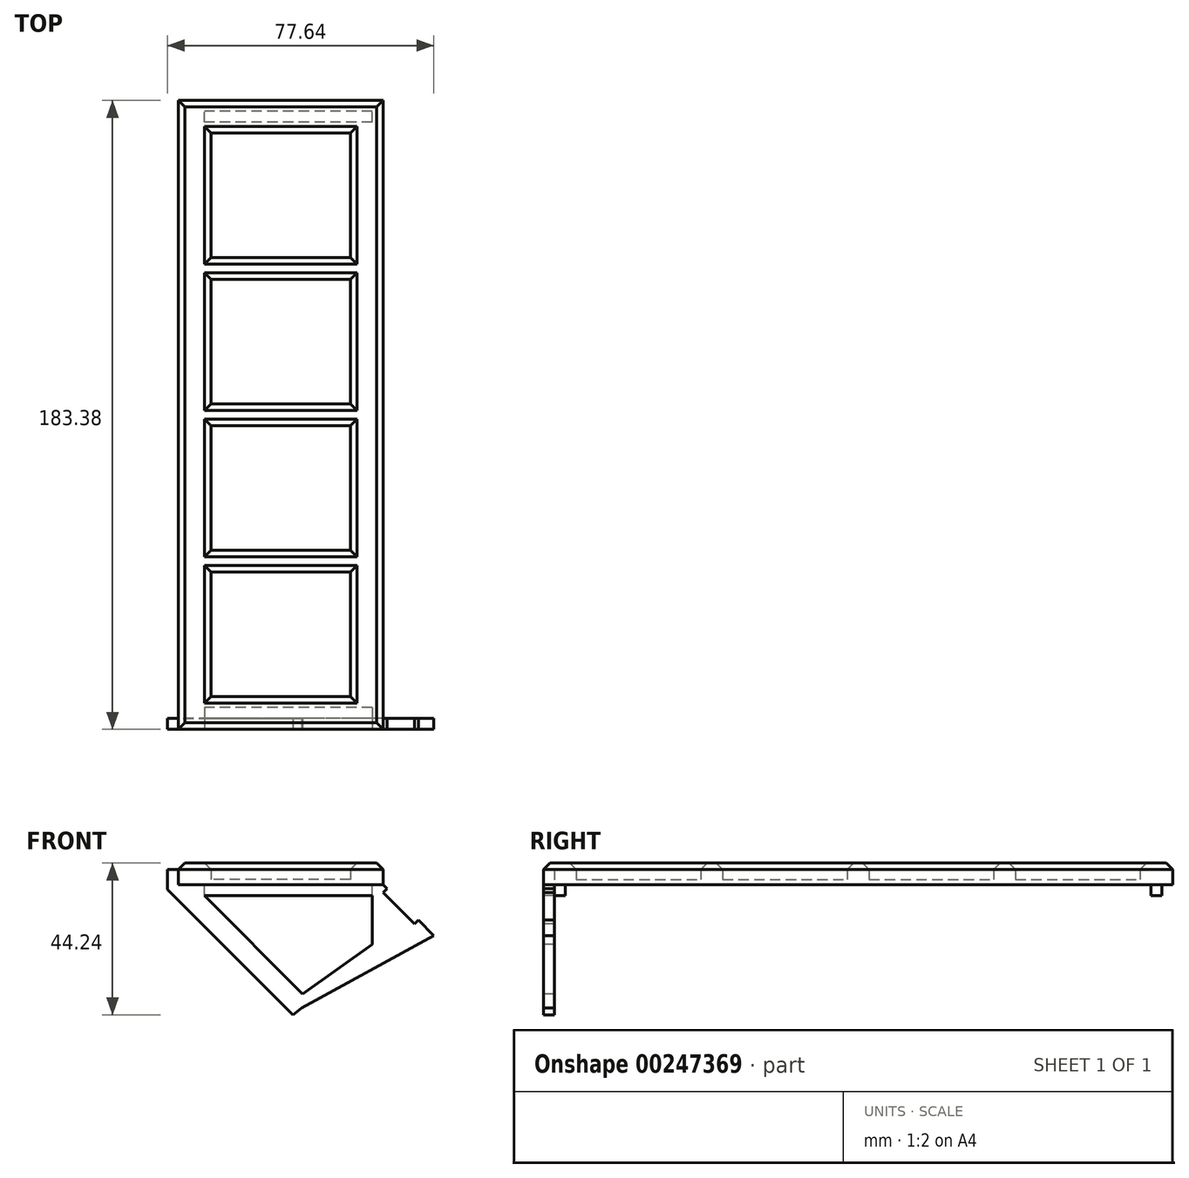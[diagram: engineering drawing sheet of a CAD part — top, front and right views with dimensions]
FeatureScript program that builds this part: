
annotation { "Feature Type Name" : "Feature", "Feature Type Description" : "" }
export const myFeature = defineFeature(function(context is Context, id is Id, definition is map)
    precondition{}
    {
        {
            var Q0;
            Q0=qCreatedBy(makeId("Top.planeOp"),FACE);
            var sketch = newSketch(context, id + "F0", { "sketchPlane" : qUnion([Q0])});
            skLineSegment(sketch, "E0.bottom", {"start": v(20.32, -82.17) * mm, "end": v(-20.32, -82.17) * mm});
            skLineSegment(sketch, "E0.top", {"start": v(20.32, 82.17) * mm, "end": v(-20.32, 82.17) * mm});
            skLineSegment(sketch, "E0.left", {"start": v(20.32, -82.17) * mm, "end": v(20.32, 82.17) * mm});
            skLineSegment(sketch, "E0.right", {"start": v(-20.32, -82.17) * mm, "end": v(-20.32, 82.17) * mm});
            skPoint(sketch, "E0.middle", {"position": v(0, 0) * mm});
            skLineSegment(sketch, "E1.0", {"start": v(-29.85, -91.7) * mm, "end": v(-29.85, 91.7) * mm});
            skLineSegment(sketch, "E1.1", {"start": v(29.84, -91.7) * mm, "end": v(-29.85, -91.7) * mm});
            skLineSegment(sketch, "E1.2", {"start": v(29.84, -91.7) * mm, "end": v(29.85, 91.7) * mm});
            skLineSegment(sketch, "E1.3", {"start": v(29.85, 91.7) * mm, "end": v(-29.85, 91.7) * mm});
            skLineSegment(sketch, "E2.0", {"start": v(20.32, -45.85) * mm, "end": v(-20.32, -45.85) * mm});
            skLineSegment(sketch, "E3.0", {"start": v(20.32, -3.18) * mm, "end": v(-20.32, -3.18) * mm});
            skLineSegment(sketch, "E4.0", {"start": v(20.32, 3.17) * mm, "end": v(-20.32, 3.17) * mm});
            skLineSegment(sketch, "E5.0", {"start": v(20.32, 39.5) * mm, "end": v(-20.32, 39.5) * mm});
            skLineSegment(sketch, "E6.0", {"start": v(20.32, 45.85) * mm, "end": v(-20.32, 45.85) * mm});
            skLineSegment(sketch, "E7.0", {"start": v(20.32, -39.5) * mm, "end": v(-20.32, -39.5) * mm});
            skSolve(sketch);
        }
        {
            var Q0;
            {var subQ5=sQuery(id+"F0.wireOp",EDGE,"E0.bottom");Q0=makeQuery(id+"F0.imprint","IMPRINT",FACE,{"disambiguationData":[TD([[makeQuery(id+"F0.imprint","IMPRINT",EDGE,{"derivedFrom":subQ5}),1.0]])]});}
            var Q1;
            {var subQ0=sQuery(id+"F0.wireOp",EDGE,"E3.0");Q1=makeQuery(id+"F0.imprint","IMPRINT",FACE,{"disambiguationData":[TD([[makeQuery(id+"F0.imprint","IMPRINT",EDGE,{"derivedFrom":subQ0}),-1.0]])]});}
            var Q2;
            {var subQ0=sQuery(id+"F0.wireOp",EDGE,"E2.0");Q2=makeQuery(id+"F0.imprint","IMPRINT",FACE,{"disambiguationData":[TD([[makeQuery(id+"F0.imprint","IMPRINT",EDGE,{"derivedFrom":subQ0}),-1.0]])]});}
            var Q3;
            {var subQ0=sQuery(id+"F0.wireOp",EDGE,"E5.0");Q3=makeQuery(id+"F0.imprint","IMPRINT",FACE,{"disambiguationData":[TD([[makeQuery(id+"F0.imprint","IMPRINT",EDGE,{"derivedFrom":subQ0}),-1.0]])]});}
            extrude(context, id + "F1", {"entities" : qUnion([Q0, Q1, Q2, Q3]), "depth" : 6.35 * mm});
        }
        {
            var Q0;
            Q0=makeQuery(id+"F1.opExtrude","CAP_FACE",FACE,{"disambiguationData":[OSD([sQuery(id+"F0.wireOp",EDGE,"E0.bottom"),sQuery(id+"F0.wireOp",EDGE,"E0.top"),sQuery(id+"F0.wireOp",EDGE,"E0.left"),sQuery(id+"F0.wireOp",EDGE,"E0.right"),sQuery(id+"F0.wireOp",EDGE,"E1.0"),sQuery(id+"F0.wireOp",EDGE,"E1.1"),sQuery(id+"F0.wireOp",EDGE,"E1.2"),sQuery(id+"F0.wireOp",EDGE,"E1.3"),sQuery(id+"F0.wireOp",EDGE,"E2.0"),sQuery(id+"F0.wireOp",EDGE,"E3.0"),sQuery(id+"F0.wireOp",EDGE,"E4.0"),sQuery(id+"F0.wireOp",EDGE,"E5.0"),sQuery(id+"F0.wireOp",EDGE,"E6.0"),sQuery(id+"F0.wireOp",EDGE,"E7.0")])],"isStart":false});
            chamfer(context, id + "F2", {"entities" : qUnion([Q0]), "width" : 1.9 * mm, "tangentPropagation" : true});
        }
        {
            var Q0;
            {var subQ0=sQuery(id+"F0.wireOp",EDGE,"E0.bottom");Q0=makeQuery(id+"F0.imprint","IMPRINT",FACE,{"disambiguationData":[TD([[makeQuery(id+"F0.imprint","IMPRINT",EDGE,{"derivedFrom":subQ0}),-1.0]])]});}
            var Q1;
            {var subQ0=sQuery(id+"F0.wireOp",EDGE,"E3.0");Q1=makeQuery(id+"F0.imprint","IMPRINT",FACE,{"disambiguationData":[TD([[makeQuery(id+"F0.imprint","IMPRINT",EDGE,{"derivedFrom":subQ0}),1.0]])]});}
            var Q2;
            {var subQ0=sQuery(id+"F0.wireOp",EDGE,"E4.0");Q2=makeQuery(id+"F0.imprint","IMPRINT",FACE,{"disambiguationData":[TD([[makeQuery(id+"F0.imprint","IMPRINT",EDGE,{"derivedFrom":subQ0}),-1.0]])]});}
            var Q3;
            {var subQ0=sQuery(id+"F0.wireOp",EDGE,"E0.top");Q3=makeQuery(id+"F0.imprint","IMPRINT",FACE,{"disambiguationData":[TD([[makeQuery(id+"F0.imprint","IMPRINT",EDGE,{"derivedFrom":subQ0}),1.0]])]});}
            extrude(context, id + "F3", {"entities" : qUnion([Q0, Q1, Q2, Q3]), "operationType" : NewBodyOperationType.ADD, "depth" : 1.59 * mm});
        }
        {
            var Q0;
            Q0=makeQuery(id+"F1.opExtrude","SWEPT_FACE",FACE,{"disambiguationData":[OSD([sQuery(id+"F0.wireOp",EDGE,"E1.1")])]});
            var sketch = newSketch(context, id + "F4", { "sketchPlane" : qUnion([Q0])});
            skLineSegment(sketch, "E8.0", {"start": v(20.32, 0) * mm, "end": v(-20.32, 0) * mm});
            skLineSegment(sketch, "E9.0", {"start": v(29.85, 0) * mm, "end": v(-29.84, 0) * mm});
            skLineSegment(sketch, "E10", {"start": v(-29.84, 0) * mm, "end": v(6.08, -35.92) * mm});
            skPoint(sketch, "E11.middle", {"position": v(29.85, -9.53) * mm});
            skPoint(sketch, "E12.0", {"position": v(29.84, 2.22) * mm});
            skLineSegment(sketch, "E13.0", {"start": v(29.84, 4.45) * mm, "end": v(29.84, 0) * mm});
            skLineSegment(sketch, "E14", {"start": v(29.85, 0) * mm, "end": v(40.13, -10.28) * mm});
            skPoint(sketch, "E15.middle", {"position": v(34.99, -5.14) * mm});
            skLineSegment(sketch, "E16", {"start": v(40.13, -10.28) * mm, "end": v(39, -11.4) * mm});
            skLineSegment(sketch, "E17", {"start": v(39, -11.4) * mm, "end": v(29.85, -2.25) * mm});
            skLineSegment(sketch, "E18", {"start": v(29.85, -2.25) * mm, "end": v(30.97, -1.12) * mm});
            skLineSegment(sketch, "E19", {"start": v(40.13, -10.28) * mm, "end": v(44.62, -14.77) * mm});
            skLineSegment(sketch, "E20", {"start": v(44.62, -14.77) * mm, "end": v(6.08, -35.92) * mm});
            skLineSegment(sketch, "E21", {"start": v(-29.85, 4.45) * mm, "end": v(-33.02, 4.45) * mm});
            skLineSegment(sketch, "E22", {"start": v(-33.02, 4.45) * mm, "end": v(-33.02, -1.32) * mm});
            skLineSegment(sketch, "E23", {"start": v(-33.02, -1.32) * mm, "end": v(3.55, -37.89) * mm});
            skLineSegment(sketch, "E24", {"start": v(3.55, -37.89) * mm, "end": v(6.08, -35.92) * mm});
            skSolve(sketch);
        }
        {
            var Q0;
            {var subQ0=sQuery(id+"F4.wireOp",EDGE,"E10");Q0=makeQuery(id+"F4.imprint","IMPRINT",FACE,{"disambiguationData":[TD([[makeQuery(id+"F4.imprint","IMPRINT",EDGE,{"derivedFrom":subQ0}),1.0]])]});}
            var Q1;
            Q1=makeQuery(id+"F4.imprint","IMPRINT",FACE,{"disambiguationData":[TD([[makeQuery(id+"F4.imprint","IMPRINT",EDGE,{"derivedFrom":sQuery(id+"F4.wireOp",EDGE,"E10")}),-1.0]])]});
            extrude(context, id + "F5", {"entities" : qUnion([Q0, Q1]), "oppositeDirection" : true, "depth" : 3.17 * mm});
        }
        {
            var Q0;
            Q0=makeQuery(id+"F5.opExtrude","CAP_FACE",FACE,{"disambiguationData":[OSD([sQuery(id+"F4.wireOp",EDGE,"E9.0"),sQuery(id+"F4.wireOp",EDGE,"E10"),sQuery(id+"F4.wireOp",EDGE,"8CqGdBqh-zlcG-GjEP-Pr5V-DbjYPcWGBq1A"),sQuery(id+"F4.wireOp",EDGE,"UwHirS80-iQ5j-kHgM-V7hk-1jNkFoblKyDJ"),sQuery(id+"F4.wireOp",EDGE,"E11.bottom"),sQuery(id+"F4.wireOp",EDGE,"E11.top"),sQuery(id+"F4.wireOp",EDGE,"E11.left")])],"isStart":true});
            var sketch = newSketch(context, id + "F6", { "sketchPlane" : qUnion([Q0])});
            skLineSegment(sketch, "E25.0", {"start": v(29.84, 0) * mm, "end": v(-29.85, 0) * mm});
            skLineSegment(sketch, "E26.0", {"start": v(-29.85, 0) * mm, "end": v(6.08, -35.92) * mm});
            skLineSegment(sketch, "E27.0", {"start": v(29.85, -19.05) * mm, "end": v(6.08, -35.92) * mm});
            skLineSegment(sketch, "E28.0", {"start": v(26.67, -17.41) * mm, "end": v(6.42, -31.78) * mm});
            skLineSegment(sketch, "E28.1", {"start": v(-22.18, -3.17) * mm, "end": v(6.42, -31.78) * mm});
            skLineSegment(sketch, "E28.2", {"start": v(26.67, -3.18) * mm, "end": v(-22.18, -3.18) * mm});
            skLineSegment(sketch, "E29", {"start": v(26.67, -3.18) * mm, "end": v(26.67, -17.41) * mm});
            skSolve(sketch);
        }
        {
            var Q0;
            Q0=makeQuery(id+"F6.imprint","IMPRINT",FACE,{"disambiguationData":[TD([[makeQuery(id+"F6.imprint","IMPRINT",EDGE,{"derivedFrom":sQuery(id+"F6.wireOp",EDGE,"E28.0")}),-1.0]])]});
            extrude(context, id + "F7", {"entities" : qUnion([Q0]), "operationType" : NewBodyOperationType.REMOVE, "oppositeDirection" : true, "depth" : 25.4 * mm});
        }
        {
            var Q0;
            Q0=makeQuery(id+"F5.opExtrude","CAP_FACE",FACE,{"disambiguationData":[OSD([sQuery(id+"F0.wireOp",EDGE,"E1.0"),sQuery(id+"F0.wireOp",EDGE,"E1.1"),sQuery(id+"F4.wireOp",EDGE,"E9.0"),sQuery(id+"F4.wireOp",EDGE,"E14"),sQuery(id+"F4.wireOp",EDGE,"E16"),sQuery(id+"F4.wireOp",EDGE,"E17"),sQuery(id+"F4.wireOp",EDGE,"E18"),sQuery(id+"F4.wireOp",EDGE,"E19"),sQuery(id+"F4.wireOp",EDGE,"E20"),sQuery(id+"F4.wireOp",EDGE,"E21"),sQuery(id+"F4.wireOp",EDGE,"E22"),sQuery(id+"F4.wireOp",EDGE,"E23"),sQuery(id+"F4.wireOp",EDGE,"E24")])],"isStart":false});
            var sketch = newSketch(context, id + "F8", { "sketchPlane" : qUnion([Q0])});
            skLineSegment(sketch, "E30.0", {"start": v(-29.84, 0) * mm, "end": v(29.85, 0) * mm});
            skLineSegment(sketch, "E31.0", {"start": v(-26.67, -3.18) * mm, "end": v(22.18, -3.18) * mm});
            skLineSegment(sketch, "E32", {"start": v(-26.67, -3.18) * mm, "end": v(-26.67, 0) * mm});
            skLineSegment(sketch, "E33", {"start": v(22.18, -3.18) * mm, "end": v(22.18, 0) * mm});
            skSolve(sketch);
        }
        {
            var Q0;
            Q0 = qSketchRegion(id + "F8", true);
            var Q1;
            Q1=makeQuery(id+"F8.imprint","IMPRINT",FACE,{"disambiguationData":[TD([[makeQuery(id+"F8.imprint","IMPRINT",EDGE,{"derivedFrom":sQuery(id+"F8.wireOp",EDGE,"E31.0")}),1.0]])]});
            extrude(context, id + "F9", {"entities" : qUnion([Q0, Q1]), "depth" : 3.17 * mm});
        }
        {
            var Q0;
            Q0=makeQuery(id+"F9.opExtrude","SWEPT_BODY",BODY,{"disambiguationData":[OSD([sQuery(id+"F8.wireOp",EDGE,"E30.0"),sQuery(id+"F8.wireOp",EDGE,"E31.0"),sQuery(id+"F8.wireOp",EDGE,"E32"),sQuery(id+"F8.wireOp",EDGE,"E33")])]});
            var Q1;
            Q1=qCreatedBy(makeId("Front.planeOp"),FACE);
            mirror(context, id + "F10", {"entities" : qUnion([Q0]), "mirrorPlane" : qUnion([Q1])});
        }
    });
